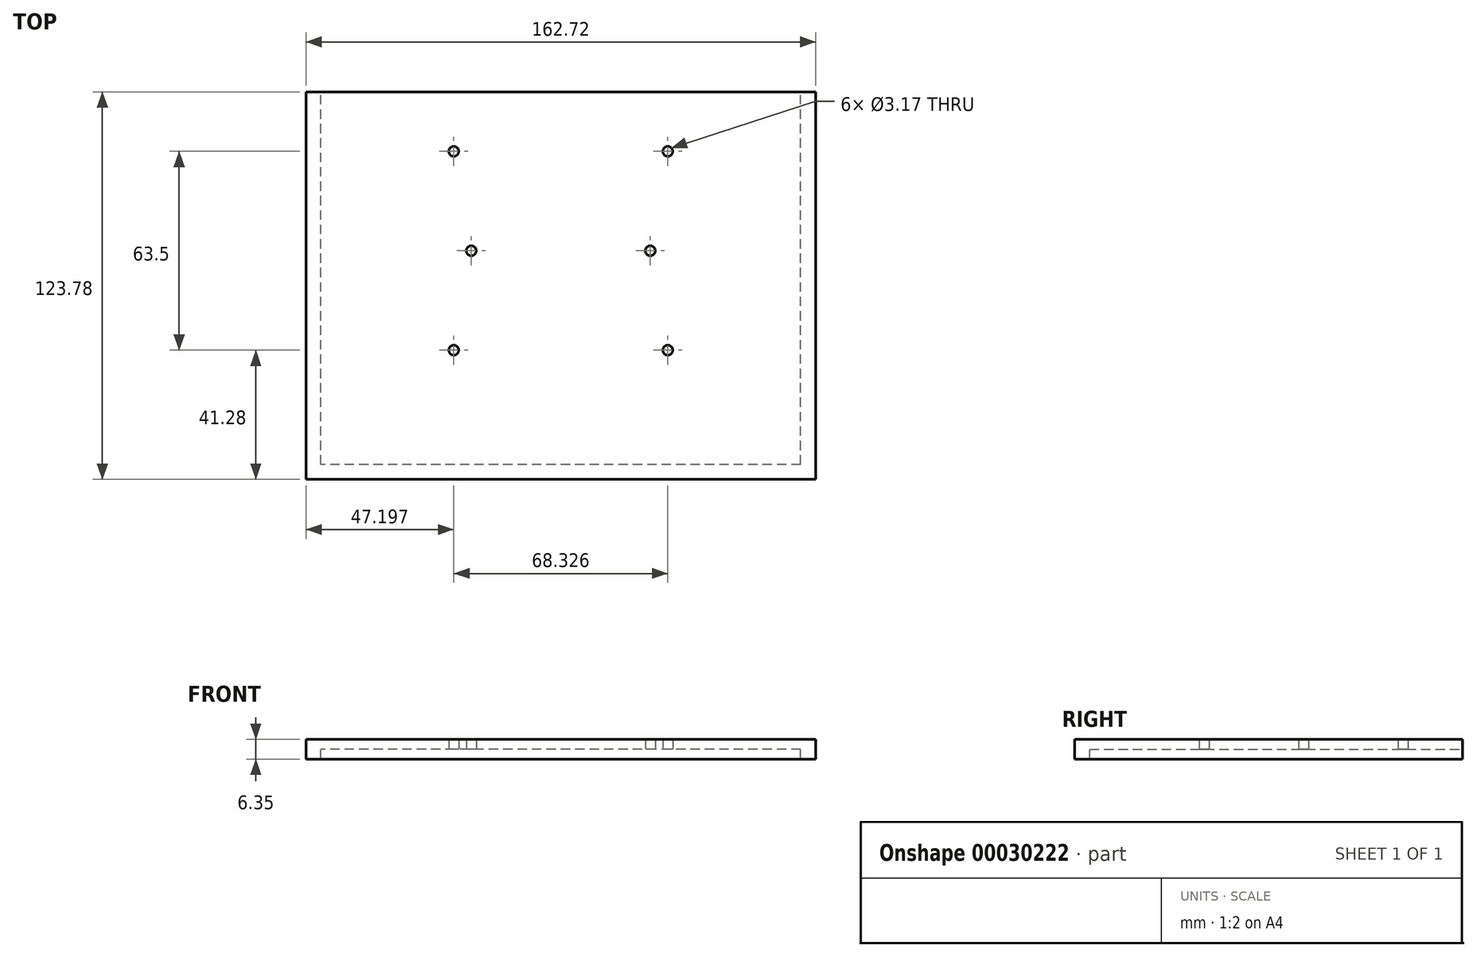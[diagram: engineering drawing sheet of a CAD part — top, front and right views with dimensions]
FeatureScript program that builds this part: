
annotation { "Feature Type Name" : "Feature", "Feature Type Description" : "" }
export const myFeature = defineFeature(function(context is Context, id is Id, definition is map)
    precondition{}
    {
        {
            var Q0;
            Q0=qCreatedBy(makeId("Top.planeOp"),FACE);
            var sketch = newSketch(context, id + "F0", { "sketchPlane" : qUnion([Q0])});
            skLineSegment(sketch, "E0.rect.bottom", {"start": v(76.6, -68.26) * mm, "end": v(-76.6, -68.26) * mm});
            skLineSegment(sketch, "E0.rect.left", {"start": v(76.6, -68.26) * mm, "end": v(76.6, 50.75) * mm});
            skLineSegment(sketch, "E0.rect.right", {"start": v(-76.6, -68.26) * mm, "end": v(-76.6, 50.75) * mm});
            skPoint(sketch, "E0.rect.middle", {"position": v(0, 0) * mm});
            skCircle(sketch, "E1", {"center": v(34.16, 31.75) * mm, "radius": 1.59 * mm});
            skCircle(sketch, "E2", {"center": v(34.16, -31.75) * mm, "radius": 1.59 * mm});
            skCircle(sketch, "E3.MirrorC", {"center": v(-34.16, 31.75) * mm, "radius": 1.59 * mm});
            skCircle(sketch, "E4.MirrorC", {"center": v(-34.16, -31.75) * mm, "radius": 1.59 * mm});
            skLineSegment(sketch, "E5", {"start": v(-76.6, 50.75) * mm, "end": v(76.6, 50.75) * mm});
            skPoint(sketch, "E6.orphan", {"position": v(-76.6, 68.26) * mm});
            skPoint(sketch, "E7.orphan", {"position": v(76.6, 68.26) * mm});
            skLineSegment(sketch, "E8", {"start": v(-76.6, 50.75) * mm, "end": v(-81.36, 50.75) * mm});
            skLineSegment(sketch, "E9", {"start": v(-81.36, 50.75) * mm, "end": v(-81.36, -73.03) * mm});
            skLineSegment(sketch, "E10", {"start": v(-81.36, -73.03) * mm, "end": v(81.36, -73.03) * mm});
            skLineSegment(sketch, "E11", {"start": v(81.36, -73.03) * mm, "end": v(81.36, 50.75) * mm});
            skLineSegment(sketch, "E12", {"start": v(81.36, 50.75) * mm, "end": v(76.6, 50.75) * mm});
            skCircle(sketch, "E13", {"center": v(-28.58, 0) * mm, "radius": 1.59 * mm});
            skCircle(sketch, "E14.MirrorC", {"center": v(28.58, 0) * mm, "radius": 1.59 * mm});
            skPoint(sketch, "E15.start.orphan", {"position": v(0, 8.75) * mm});
            skSolve(sketch);
        }
        {
            var Q0;
            Q0=makeQuery(id+"F0.imprint","IMPRINT",FACE,{"disambiguationData":[TD([[makeQuery(id+"F0.imprint","IMPRINT",EDGE,{"derivedFrom":sQuery(id+"F0.wireOp",EDGE,"E0.rect.bottom")}),1.0]])]});
            var Q1;
            Q1=makeQuery(id+"F0.imprint","IMPRINT",FACE,{"disambiguationData":[TD([[makeQuery(id+"F0.imprint","IMPRINT",EDGE,{"derivedFrom":sQuery(id+"F0.wireOp",EDGE,"E0.rect.bottom")}),-1.0]])]});
            extrude(context, id + "F1", {"entities" : qUnion([Q0, Q1]), "depth" : 3.17 * mm});
        }
        {
            var Q0;
            Q0=makeQuery(id+"F0.imprint","IMPRINT",FACE,{"disambiguationData":[TD([[makeQuery(id+"F0.imprint","IMPRINT",EDGE,{"derivedFrom":sQuery(id+"F0.wireOp",EDGE,"E0.rect.bottom")}),1.0]])]});
            extrude(context, id + "F2", {"entities" : qUnion([Q0]), "operationType" : NewBodyOperationType.ADD, "oppositeDirection" : true, "depth" : 3.17 * mm});
        }
    });
